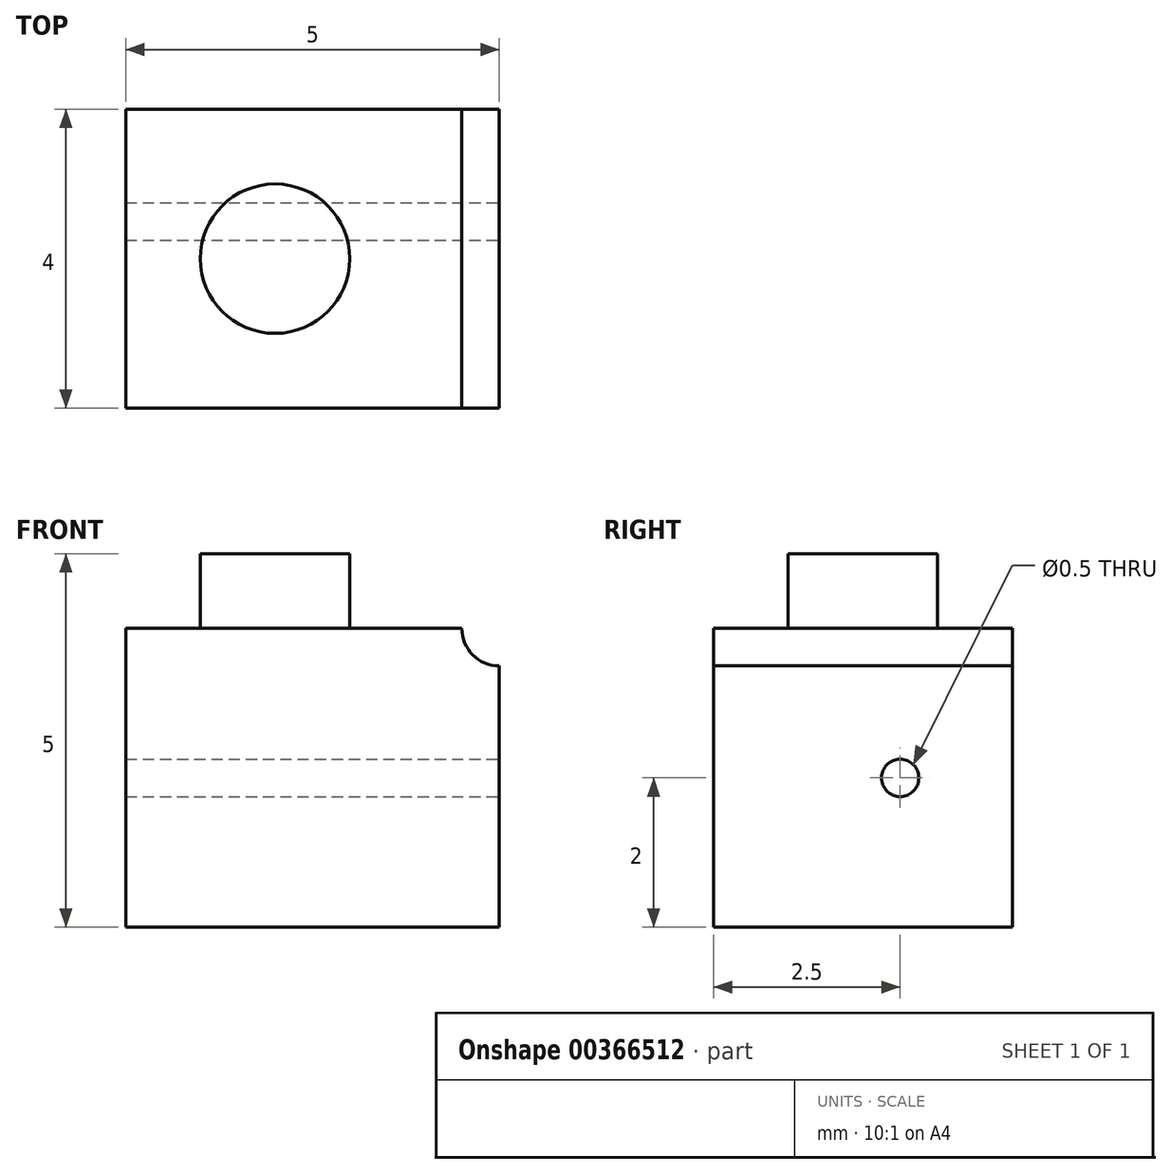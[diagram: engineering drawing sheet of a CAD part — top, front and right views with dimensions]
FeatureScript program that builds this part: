
annotation { "Feature Type Name" : "Feature", "Feature Type Description" : "" }
export const myFeature = defineFeature(function(context is Context, id is Id, definition is map)
    precondition{}
    {
        {
            var Q0;
            Q0=qCreatedBy(makeId("Top.planeOp"),FACE);
            var sketch = newSketch(context, id + "F0", { "sketchPlane" : qUnion([Q0])});
            skLineSegment(sketch, "E0", {"start": v(0, 0) * mm, "end": v(5, 0) * mm});
            skLineSegment(sketch, "E1", {"start": v(5, 0) * mm, "end": v(5, 4) * mm});
            skLineSegment(sketch, "E2", {"start": v(5, 4) * mm, "end": v(0, 4) * mm});
            skLineSegment(sketch, "E3", {"start": v(0, 4) * mm, "end": v(0, 0) * mm});
            skLineSegment(sketch, "E4", {"start": v(0, 4) * mm, "end": v(2, 4) * mm});
            skLineSegment(sketch, "E5", {"start": v(0, 4) * mm, "end": v(0, 2) * mm});
            skSolve(sketch);
        }
        {
            var Q0;
            Q0=makeQuery(id+"F0.imprint","IMPRINT",FACE,{"disambiguationData":[TD([[makeQuery(id+"F0.imprint","IMPRINT",EDGE,{"derivedFrom":sQuery(id+"F0.wireOp",EDGE,"E0")}),1.0]])]});
            extrude(context, id + "F1", {"entities" : qUnion([Q0]), "depth" : 4 * mm});
        }
        {
            var Q0;
            Q0=makeQuery(id+"F1.opExtrude","CAP_FACE",FACE,{"disambiguationData":[OSD([sQuery(id+"F0.wireOp",EDGE,"E0"),sQuery(id+"F0.wireOp",EDGE,"E1"),sQuery(id+"F0.wireOp",EDGE,"E2"),sQuery(id+"F0.wireOp",EDGE,"E3"),sQuery(id+"F0.wireOp",EDGE,"E4"),sQuery(id+"F0.wireOp",EDGE,"E5")])],"isStart":false});
            var sketch = newSketch(context, id + "F2", { "sketchPlane" : qUnion([Q0])});
            skLineSegment(sketch, "E6", {"start": v(0, 4) * mm, "end": v(2, 4) * mm});
            skLineSegment(sketch, "E7", {"start": v(0, 2) * mm, "end": v(2, 2) * mm});
            skCircle(sketch, "E8", {"center": v(2, 2) * mm, "radius": 1 * mm});
            skSolve(sketch);
        }
        {
            var Q0;
            Q0=qSketchRegion(id+"F2",true);
            extrude(context, id + "F3", {"entities" : qUnion([Q0]), "operationType" : NewBodyOperationType.ADD, "depth" : 1 * mm});
        }
        {
            var Q0;
            Q0=makeQuery(id+"F1.opExtrude","SWEPT_FACE",FACE,{"disambiguationData":[OSD([sQuery(id+"F0.wireOp",EDGE,"E2"),sQuery(id+"F0.wireOp",EDGE,"E4")])]});
            var sketch = newSketch(context, id + "F4", { "sketchPlane" : qUnion([Q0])});
            skCircle(sketch, "E9", {"center": v(-5, 4) * mm, "radius": 0.5 * mm});
            skSolve(sketch);
        }
        {
            var Q0;
            Q0=qSketchRegion(id+"F4",true);
            extrude(context, id + "F5", {"entities" : qUnion([Q0]), "operationType" : NewBodyOperationType.REMOVE, "oppositeDirection" : true, "depth" : 4 * mm});
        }
        {
            var Q0;
            Q0=makeQuery(id+"F1.opExtrude","SWEPT_FACE",FACE,{"disambiguationData":[OSD([sQuery(id+"F0.wireOp",EDGE,"E1")])]});
            var sketch = newSketch(context, id + "F6", { "sketchPlane" : qUnion([Q0])});
            skLineSegment(sketch, "E10", {"start": v(4, 3.5) * mm, "end": v(4, 2) * mm});
            skLineSegment(sketch, "E11", {"start": v(4, 2) * mm, "end": v(2.5, 2) * mm});
            skCircle(sketch, "E12", {"center": v(2.5, 2) * mm, "radius": 0.25 * mm});
            skSolve(sketch);
        }
        {
            var Q0;
            Q0=qSketchRegion(id+"F6",true);
            extrude(context, id + "F7", {"entities" : qUnion([Q0]), "operationType" : NewBodyOperationType.REMOVE, "oppositeDirection" : true, "depth" : 25 * mm});
        }
    });
